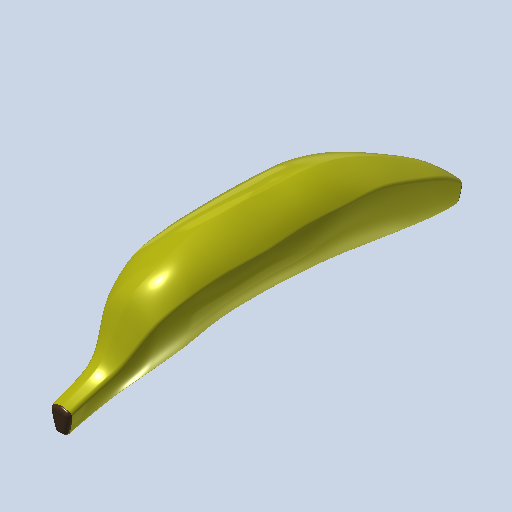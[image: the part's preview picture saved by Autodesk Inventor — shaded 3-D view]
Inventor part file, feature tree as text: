
AUTODESK INVENTOR PART (.ipt)
format: ipt  version: 2022 (Build 260153000, 153)  size: 785,920 bytes
history: native  units: mm
features: sketch x13, plane x12, fillet x3, loft x1
ambient origin geometry x8: Origin, YZ Plane, XZ Plane, XY Plane, X Axis, Y Axis, Z Axis, Center Point
bodies: Volumenkörper1 (feature_tree)
feature tree (29):
  sketch  "Skizze1"  dims[d0=20.0mm d1=20.0mm d2=20.0mm d3=20.0mm d4=20.0mm]
  plane  "Arbeitsebene1"
  sketch  "Skizze2"  dims[d5=10.0mm]
  plane  "Arbeitsebene2"
  sketch  "Skizze3"  dims[d6=-20.0mm]
  plane  "Arbeitsebene3"
  sketch  "Skizze4"  dims[d7=-15.0mm]
  plane  "Arbeitsebene4"
  sketch  "Skizze5"  dims[d8=-15.0mm]
  plane  "Arbeitsebene5"
  sketch  "Skizze6"  dims[d9=-15.0mm]
  plane  "Arbeitsebene6"
  sketch  "Skizze7"  dims[d10=-15.0mm]
  plane  "Arbeitsebene7"
  sketch  "Skizze8"  dims[d11=-6.75mm]
  plane  "Arbeitsebene8"
  sketch  "Skizze9"  dims[d12=0.0mm d13=90.0deg]
  plane  "Arbeitsebene9"
  sketch  "Skizze10"  dims[d14=0.0mm d15=90.0deg]
  plane  "Arbeitsebene10"
  sketch  "Skizze11"  dims[d16=0.0mm d17=90.0deg]
  plane  "Arbeitsebene11"
  sketch  "Skizze12"  dims[d18=0.0mm d19=90.0deg]
  plane  "Arbeitsebene12"
  loft  "Erhebung1"
  fillet  "Rundung1"  Radius=20.0mm
  fillet  "Rundung2"  Radius=20.0mm
  fillet  "Rundung4"  Radius=20.0mm
  sketch  "Skizze13"  dims[d20=0.0mm d21=90.0deg d22=0.0mm d23=90.0deg d24=0.0mm d25=90.0deg d26=0.0mm d27=90.0deg d28=0.0mm d29=90.0deg d30=0.0mm d31=90.0deg d32=0.0mm d33=90.0deg d34=0.0mm d35=90.0deg d36=0.0mm d37=90.0deg d38=2.0mm d39=2.0mm d41=2.0mm]
